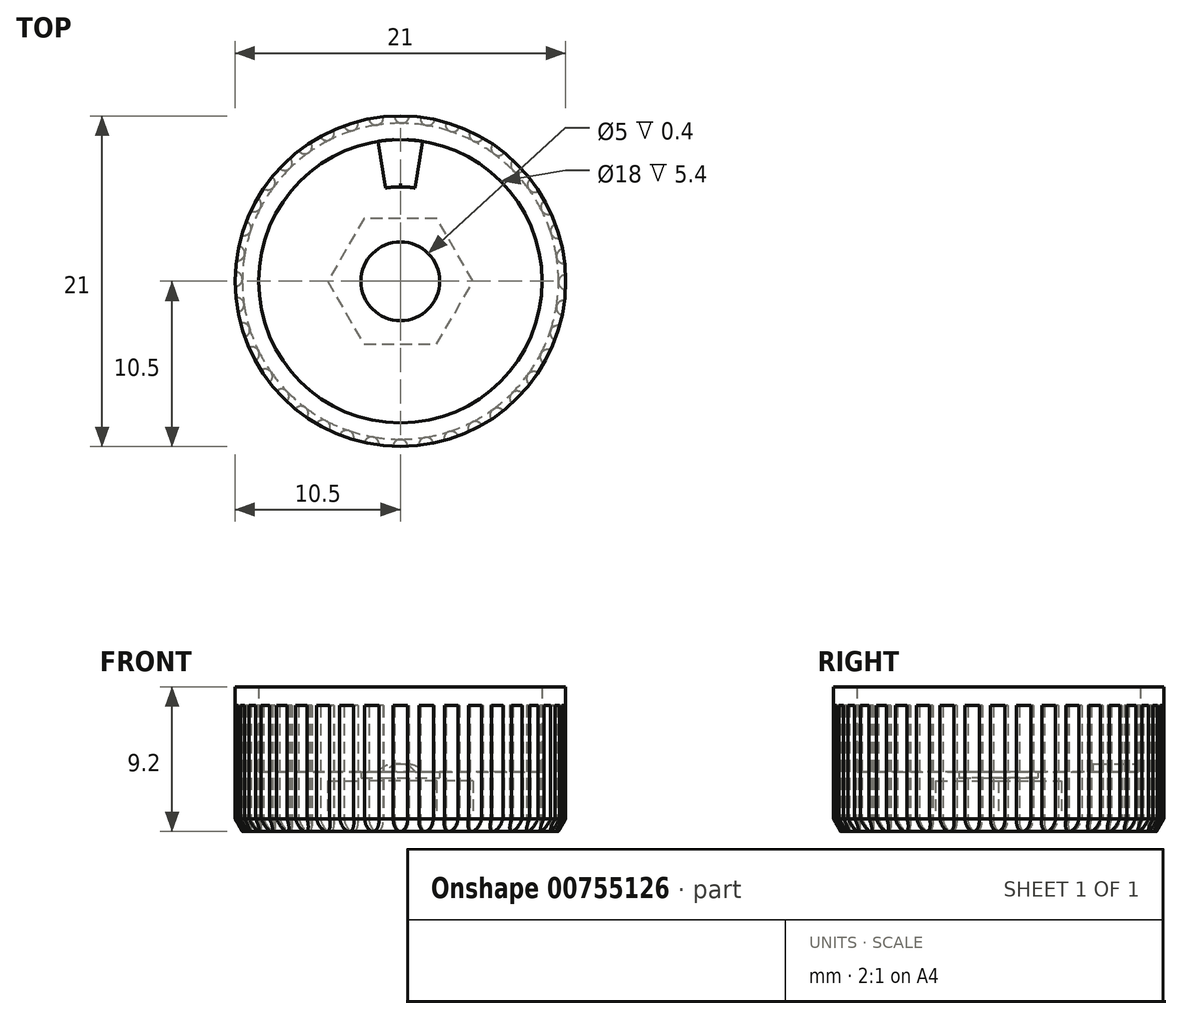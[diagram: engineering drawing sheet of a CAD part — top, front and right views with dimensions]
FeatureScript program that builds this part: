
annotation { "Feature Type Name" : "Feature", "Feature Type Description" : "" }
export const myFeature = defineFeature(function(context is Context, id is Id, definition is map)
    precondition{}
    {
        {
            var Q0;
            Q0=qCreatedBy(makeId("Front.planeOp"),FACE);
            var sketch = newSketch(context, id + "F0", { "sketchPlane" : qUnion([Q0])});
            skLineSegment(sketch, "E0", {"start": v(0, 0) * mm, "end": v(9, 0) * mm});
            skLineSegment(sketch, "E1", {"start": v(9, 0) * mm, "end": v(9, 5.4) * mm});
            skLineSegment(sketch, "E2", {"start": v(9, 5.4) * mm, "end": v(10.5, 5.4) * mm});
            skLineSegment(sketch, "E3", {"start": v(10.5, -3) * mm, "end": v(0, -3) * mm});
            skLineSegment(sketch, "E4", {"start": v(10.5, 5.4) * mm, "end": v(10.5, -3) * mm});
            skLineSegment(sketch, "E5", {"start": v(0, -3) * mm, "end": v(0, 0) * mm});
            skSolve(sketch);
        }
        {
            var Q0;
            Q0=makeQuery(id+"F0.imprint","IMPRINT",FACE,{"disambiguationData":[TD([[makeQuery(id+"F0.imprint","IMPRINT",EDGE,{"derivedFrom":sQuery(id+"F0.wireOp",EDGE,"E0")}),-1.0]])]});
            var Q1;
            Q1=sQuery(id+"F0.wireOp",EDGE,"E5");
            revolve(context, id + "F1", {"surfaceOperationType" : NewSurfaceOperationType.NEW, "entities" : qUnion([Q0]), "axis" : qUnion([Q1]), "revolveType" : RevolveType.FULL});
        }
        {
            var Q0;
            Q0=makeQuery(id+"F1.opRevolve","SWEPT_FACE",FACE,{"disambiguationData":[OSD([sQuery(id+"F0.wireOp",EDGE,"E3")])]});
            var sketch = newSketch(context, id + "F2", { "sketchPlane" : qUnion([Q0])});
            skCircle(sketch, "E6", {"center": v(0, 0) * mm, "radius": 2.5 * mm});
            skCircle(sketch, "E7.cCircle", {"center": v(0, 0) * mm, "radius": 4 * mm, "construction": true});
            skLineSegment(sketch, "E7.0", {"start": v(2.3, -4) * mm, "end": v(-2.3, -4) * mm});
            skLineSegment(sketch, "E7.1", {"start": v(-2.3, -4) * mm, "end": v(-4.62, 0) * mm});
            skLineSegment(sketch, "E7.2", {"start": v(-4.62, 0) * mm, "end": v(-2.3, 4) * mm});
            skLineSegment(sketch, "E7.3", {"start": v(-2.3, 4) * mm, "end": v(2.3, 4) * mm});
            skLineSegment(sketch, "E7.4", {"start": v(2.3, 4) * mm, "end": v(4.62, 0) * mm});
            skLineSegment(sketch, "E7.5", {"start": v(4.62, 0) * mm, "end": v(2.3, -4) * mm});
            skPoint(sketch, "E7.0.midPoint", {"position": v(0, -4) * mm});
            skSolve(sketch);
        }
        {
            var Q0;
            Q0=makeQuery(id+"F2.imprint","IMPRINT",FACE,{"disambiguationData":[TD([[makeQuery(id+"F2.imprint","IMPRINT",EDGE,{"derivedFrom":sQuery(id+"F2.wireOp",EDGE,"E6")}),1.0]])]});
            extrude(context, id + "F3", {"entities" : qUnion([Q0]), "operationType" : NewBodyOperationType.REMOVE, "endBound" : BoundingType.THROUGH_ALL, "oppositeDirection" : true, "depth" : 25 * mm, "offsetDistance" : 25 * mm});
        }
        {
            var Q0;
            Q0=makeQuery(id+"F2.imprint","IMPRINT",FACE,{"disambiguationData":[TD([[makeQuery(id+"F2.imprint","IMPRINT",EDGE,{"derivedFrom":sQuery(id+"F2.wireOp",EDGE,"E6")}),-1.0]])]});
            extrude(context, id + "F4", {"entities" : qUnion([Q0]), "operationType" : NewBodyOperationType.REMOVE, "oppositeDirection" : true, "depth" : 2.4 * mm, "offsetDistance" : 25 * mm});
        }
        {
            var Q0;
            Q0=makeQuery(id+"F2.imprint","IMPRINT",FACE,{"disambiguationData":[TD([[makeQuery(id+"F2.imprint","IMPRINT",EDGE,{"derivedFrom":sQuery(id+"F2.wireOp",EDGE,"E7.0")}),1.0]])]});
            var Q1;
            Q1=makeQuery(id+"F2.imprint","IMPRINT",FACE,{"disambiguationData":[TD([[makeQuery(id+"F2.imprint","IMPRINT",EDGE,{"derivedFrom":sQuery(id+"F2.wireOp",EDGE,"E6")}),-1.0]])]});
            var Q2;
            Q2=makeQuery(id+"F2.imprint","IMPRINT",FACE,{"disambiguationData":[TD([[makeQuery(id+"F2.imprint","IMPRINT",EDGE,{"derivedFrom":sQuery(id+"F2.wireOp",EDGE,"E6")}),1.0]])]});
            extrude(context, id + "F5", {"entities" : qUnion([Q0, Q1, Q2]), "depth" : 0.8 * mm, "offsetDistance" : 25 * mm, "hasDraft" : true, "draftAngle" : 30 * degree, "draftPullDirection" : true});
        }
        {
            var Q0;
            Q0=makeQuery(id+"F1.opRevolve","SWEPT_FACE",FACE,{"disambiguationData":[OSD([sQuery(id+"F0.wireOp",EDGE,"E0")])]});
            var sketch = newSketch(context, id + "F6", { "sketchPlane" : qUnion([Q0])});
            skCircle(sketch, "E8", {"center": v(0, 0) * mm, "radius": 6 * mm});
            skLineSegment(sketch, "E9", {"start": v(-0.94, 5.93) * mm, "end": v(-1.41, 8.89) * mm});
            skLineSegment(sketch, "E10", {"start": v(0.94, 5.93) * mm, "end": v(1.41, 8.89) * mm});
            skSolve(sketch);
        }
        {
            var Q0;
            {var subQ0=sQuery(id+"F6.wireOp",EDGE,"E9");Q0=makeQuery(id+"F6.imprint","IMPRINT",FACE,{"disambiguationData":[TD([[makeQuery(id+"F6.imprint","IMPRINT",EDGE,{"derivedFrom":subQ0}),-1.0]])]});}
            extrude(context, id + "F7", {"entities" : qUnion([Q0]), "operationType" : NewBodyOperationType.ADD, "depth" : 0.5 * mm, "offsetDistance" : 25 * mm});
        }
        {
            var Q0;
            Q0=makeQuery(id+"F7.opExtrude","CAP_EDGE",EDGE,{"disambiguationData":[OSD([sQuery(id+"F6.wireOp",EDGE,"E9")])],"isStart":false});
            var Q1;
            Q1=makeQuery(id+"F7.opExtrude","CAP_EDGE",EDGE,{"disambiguationData":[OSD([sQuery(id+"F6.wireOp",EDGE,"E10")])],"isStart":false});
            fillet(context, id + "F8", {"entities" : qUnion([Q0, Q1]), "radius" : 1.2 * mm, "tangentPropagation" : true, "allowEdgeOverflow" : false});
        }
        {
            var Q0;
            Q0=makeQuery(id+"F5.opExtrude","CAP_FACE",FACE,{"disambiguationData":[OSD([sQuery(id+"F0.wireOp",EDGE,"E3"),sQuery(id+"F0.wireOp",EDGE,"E4")])],"isStart":false});
            var sketch = newSketch(context, id + "F9", { "sketchPlane" : qUnion([Q0])});
            skCircle(sketch, "E11", {"center": v(0, 10.5) * mm, "radius": 0.46 * mm});
            skCircle(sketch, "E12.1.0", {"center": v(1.64, 10.37) * mm, "radius": 0.46 * mm});
            skCircle(sketch, "E12.2.0", {"center": v(3.24, 9.99) * mm, "radius": 0.46 * mm});
            skCircle(sketch, "E12.3.0", {"center": v(4.75, 9.36) * mm, "radius": 0.46 * mm});
            skCircle(sketch, "E12.4.0", {"center": v(6.16, 8.5) * mm, "radius": 0.46 * mm});
            skCircle(sketch, "E12.5.0", {"center": v(7.4, 7.44) * mm, "radius": 0.46 * mm});
            skCircle(sketch, "E12.6.0", {"center": v(8.48, 6.2) * mm, "radius": 0.46 * mm});
            skCircle(sketch, "E12.7.0", {"center": v(9.34, 4.8) * mm, "radius": 0.46 * mm});
            skCircle(sketch, "E12.8.0", {"center": v(9.97, 3.28) * mm, "radius": 0.46 * mm});
            skCircle(sketch, "E12.9.0", {"center": v(10.36, 1.68) * mm, "radius": 0.46 * mm});
            skCircle(sketch, "E12.10.0", {"center": v(10.5, 0.05) * mm, "radius": 0.46 * mm});
            skCircle(sketch, "E12.11.0", {"center": v(10.38, -1.6) * mm, "radius": 0.46 * mm});
            skCircle(sketch, "E12.12.0", {"center": v(10, -3.2) * mm, "radius": 0.46 * mm});
            skCircle(sketch, "E12.13.0", {"center": v(9.38, -4.71) * mm, "radius": 0.46 * mm});
            skCircle(sketch, "E12.14.0", {"center": v(8.53, -6.12) * mm, "radius": 0.46 * mm});
            skCircle(sketch, "E12.15.0", {"center": v(7.47, -7.37) * mm, "radius": 0.46 * mm});
            skCircle(sketch, "E12.16.0", {"center": v(6.23, -8.45) * mm, "radius": 0.46 * mm});
            skCircle(sketch, "E12.17.0", {"center": v(4.84, -9.32) * mm, "radius": 0.46 * mm});
            skCircle(sketch, "E12.18.0", {"center": v(3.33, -9.96) * mm, "radius": 0.46 * mm});
            skCircle(sketch, "E12.19.0", {"center": v(1.73, -10.36) * mm, "radius": 0.46 * mm});
            skCircle(sketch, "E12.20.0", {"center": v(0.1, -10.5) * mm, "radius": 0.46 * mm});
            skCircle(sketch, "E12.21.0", {"center": v(-1.55, -10.39) * mm, "radius": 0.46 * mm});
            skCircle(sketch, "E12.22.0", {"center": v(-3.15, -10.02) * mm, "radius": 0.46 * mm});
            skCircle(sketch, "E12.23.0", {"center": v(-4.67, -9.4) * mm, "radius": 0.46 * mm});
            skCircle(sketch, "E12.24.0", {"center": v(-6.08, -8.56) * mm, "radius": 0.46 * mm});
            skCircle(sketch, "E12.25.0", {"center": v(-7.34, -7.5) * mm, "radius": 0.46 * mm});
            skCircle(sketch, "E12.26.0", {"center": v(-8.42, -6.27) * mm, "radius": 0.46 * mm});
            skCircle(sketch, "E12.27.0", {"center": v(-9.3, -4.88) * mm, "radius": 0.46 * mm});
            skCircle(sketch, "E12.28.0", {"center": v(-9.94, -3.37) * mm, "radius": 0.46 * mm});
            skCircle(sketch, "E12.29.0", {"center": v(-10.35, -1.78) * mm, "radius": 0.46 * mm});
            skCircle(sketch, "E12.30.0", {"center": v(-10.5, -0.14) * mm, "radius": 0.46 * mm});
            skCircle(sketch, "E12.31.0", {"center": v(-10.4, 1.5) * mm, "radius": 0.46 * mm});
            skCircle(sketch, "E12.32.0", {"center": v(-10.03, 3.1) * mm, "radius": 0.46 * mm});
            skCircle(sketch, "E12.33.0", {"center": v(-9.42, 4.63) * mm, "radius": 0.46 * mm});
            skCircle(sketch, "E12.34.0", {"center": v(-8.59, 6.04) * mm, "radius": 0.46 * mm});
            skCircle(sketch, "E12.35.0", {"center": v(-7.54, 7.3) * mm, "radius": 0.46 * mm});
            skCircle(sketch, "E12.36.0", {"center": v(-6.3, 8.4) * mm, "radius": 0.46 * mm});
            skCircle(sketch, "E12.37.0", {"center": v(-4.92, 9.28) * mm, "radius": 0.46 * mm});
            skCircle(sketch, "E12.38.0", {"center": v(-3.41, 9.93) * mm, "radius": 0.46 * mm});
            skCircle(sketch, "E12.39.0", {"center": v(-1.82, 10.34) * mm, "radius": 0.46 * mm});
            skPoint(sketch, "E12.center", {"position": v(0, 0) * mm});
            skLineSegment(sketch, "E12.anchor1", {"start": v(0, 0) * mm, "end": v(0, 10.5) * mm, "construction": true});
            skLineSegment(sketch, "E12.anchor2", {"start": v(0, 0) * mm, "end": v(-1.82, 10.34) * mm, "construction": true});
            skSolve(sketch);
        }
        {
            var Q0;
            Q0 = qSketchRegion(id + "F9", true);
            extrude(context, id + "F10", {"entities" : qUnion([Q0]), "operationType" : NewBodyOperationType.REMOVE, "oppositeDirection" : true, "depth" : 8 * mm, "offsetDistance" : 25 * mm});
        }
        {
            var Q0;
            Q0=makeQuery(id+"F4.boolean.opBoolean","COPY",FACE,{"derivedFrom":makeQuery(id+"F4.opExtrude","CAP_FACE",FACE,{"disambiguationData":[OSD([sQuery(id+"F2.wireOp",EDGE,"E6"),sQuery(id+"F2.wireOp",EDGE,"E7.0"),sQuery(id+"F2.wireOp",EDGE,"E7.1"),sQuery(id+"F2.wireOp",EDGE,"E7.2"),sQuery(id+"F2.wireOp",EDGE,"E7.3"),sQuery(id+"F2.wireOp",EDGE,"E7.4"),sQuery(id+"F2.wireOp",EDGE,"E7.5")])],"isStart":false})});
            var sketch = newSketch(context, id + "F11", { "sketchPlane" : qUnion([Q0])});
            skCircle(sketch, "E13.0", {"center": v(0, 0) * mm, "radius": 2.5 * mm});
            skSolve(sketch);
        }
        {
            var Q0;
            Q0=makeQuery(id+"F11.imprint","IMPRINT",FACE,{"disambiguationData":[TD([[makeQuery(id+"F11.imprint","IMPRINT",EDGE,{"derivedFrom":sQuery(id+"F11.wireOp",EDGE,"E13.0")}),1.0]])]});
            extrude(context, id + "F12", {"entities" : qUnion([Q0]), "operationType" : NewBodyOperationType.ADD, "oppositeDirection" : true, "depth" : 0.2 * mm, "offsetDistance" : 25 * mm});
        }
    });
